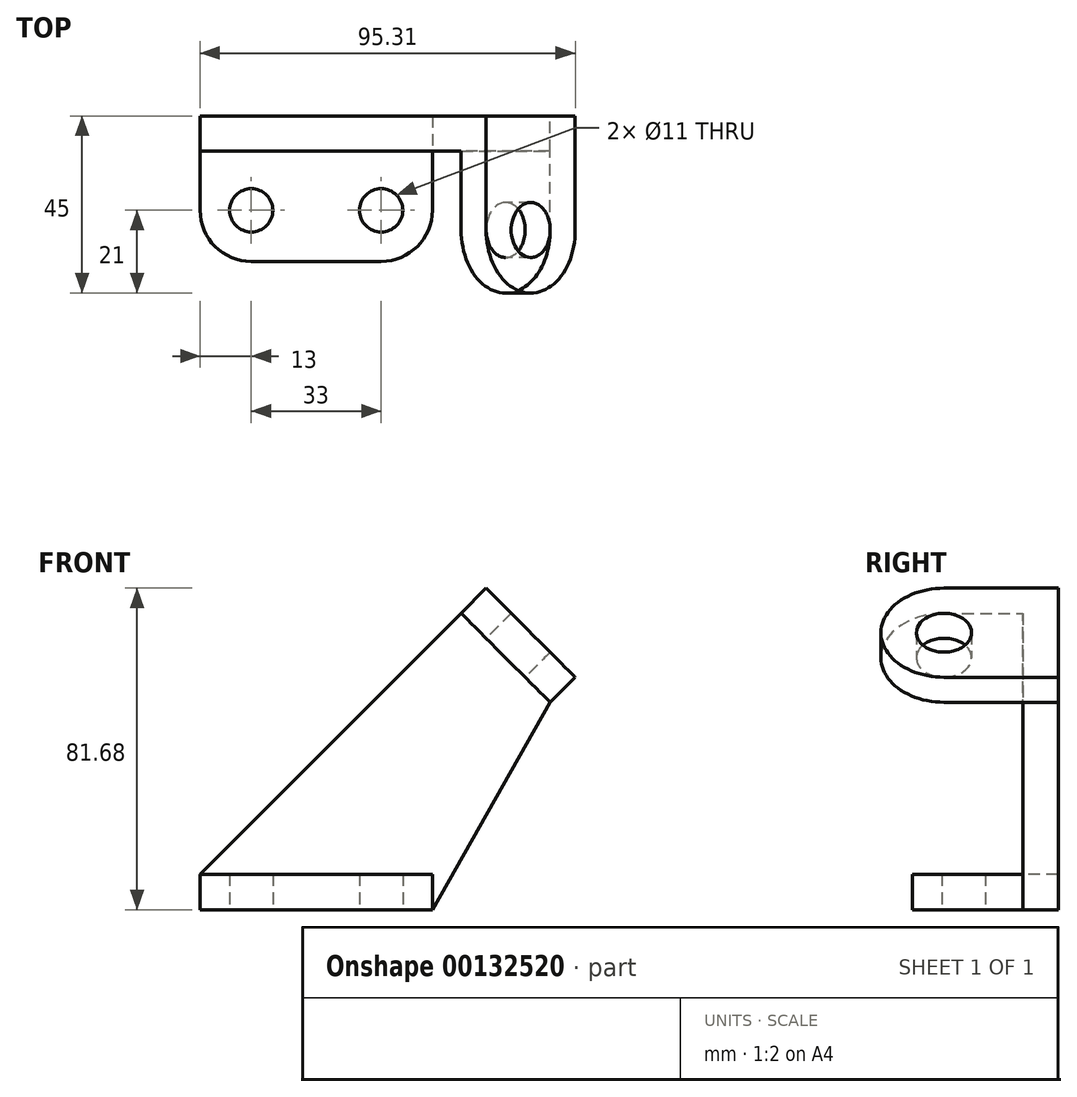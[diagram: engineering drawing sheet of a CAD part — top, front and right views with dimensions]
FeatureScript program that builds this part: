
annotation { "Feature Type Name" : "Feature", "Feature Type Description" : "" }
export const myFeature = defineFeature(function(context is Context, id is Id, definition is map)
    precondition{}
    {
        {
            var Q0;
            Q0=qCreatedBy(makeId("Top.planeOp"),FACE);
            var sketch = newSketch(context, id + "F0", { "sketchPlane" : qUnion([Q0])});
            skCircle(sketch, "E0", {"center": v(0, 0) * mm, "radius": 5.5 * mm});
            skCircle(sketch, "E1", {"center": v(33, 0) * mm, "radius": 5.5 * mm});
            skLineSegment(sketch, "E2", {"start": v(-13, 24) * mm, "end": v(-13, 0) * mm});
            skLineSegment(sketch, "E3", {"start": v(46, 24) * mm, "end": v(46, 0) * mm});
            skArc(sketch, "E4", {"start": v(-13, 0) * mm, "mid": v(-9.2, -9.2) * mm, "end": v(0, -13) * mm});
            skArc(sketch, "E5", {"start": v(33, -13) * mm, "mid": v(42.2, -9.2) * mm, "end": v(46, 0) * mm});
            skLineSegment(sketch, "E6", {"start": v(-13, 24) * mm, "end": v(46, 24) * mm});
            skLineSegment(sketch, "E7", {"start": v(0, -13) * mm, "end": v(33, -13) * mm});
            skSolve(sketch);
        }
        {
            var Q0;
            Q0 = qSketchRegion(id + "F0", true);
            extrude(context, id + "F1", {"entities" : qUnion([Q0]), "depth" : 9 * mm});
        }
        {
            var Q0;
            Q0=makeQuery(id+"F1.opExtrude","SWEPT_FACE",FACE,{"disambiguationData":[OSD([sQuery(id+"F0.wireOp",EDGE,"E6")])]});
            var sketch = newSketch(context, id + "F2", { "sketchPlane" : qUnion([Q0])});
            skPoint(sketch, "E8.0", {"position": v(13, 9) * mm});
            skLineSegment(sketch, "E9", {"start": v(13, 9) * mm, "end": v(-53.31, 75.31) * mm});
            skLineSegment(sketch, "E10", {"start": v(-53.31, 75.31) * mm, "end": v(-75.94, 52.69) * mm});
            skLineSegment(sketch, "E11", {"start": v(-46, 9) * mm, "end": v(13, 9) * mm});
            skLineSegment(sketch, "E12", {"start": v(-75.94, 52.69) * mm, "end": v(-46, 0) * mm});
            skLineSegment(sketch, "E13", {"start": v(-64.63, 64) * mm, "end": v(0, 64) * mm, "construction": true});
            skSolve(sketch);
        }
        {
            var Q0;
            Q0=makeQuery(id+"F2.imprint","IMPRINT",FACE,{"disambiguationData":[TD([[makeQuery(id+"F2.imprint","IMPRINT",EDGE,{"derivedFrom":sQuery(id+"F2.wireOp",EDGE,"E9")}),1.0]])]});
            extrude(context, id + "F3", {"entities" : qUnion([Q0]), "operationType" : NewBodyOperationType.ADD, "oppositeDirection" : true, "depth" : 9 * mm});
        }
        {
            var Q0;
            Q0=makeQuery(id+"F3.opExtrude","SWEPT_FACE",FACE,{"disambiguationData":[OSD([sQuery(id+"F2.wireOp",EDGE,"E10")])]});
            var sketch = newSketch(context, id + "F4", { "sketchPlane" : qUnion([Q0])});
            skLineSegment(sketch, "E14", {"start": v(24, 15.56) * mm, "end": v(-5, 15.56) * mm});
            skArc(sketch, "E15", {"start": v(-5, 15.56) * mm, "mid": v(-21, -0.44) * mm, "end": v(-5, -16.44) * mm});
            skLineSegment(sketch, "E16", {"start": v(24, -16.44) * mm, "end": v(-5, -16.44) * mm});
            skLineSegment(sketch, "E17", {"start": v(24, 15.56) * mm, "end": v(24, -16.44) * mm});
            skCircle(sketch, "E18", {"center": v(-5, -0.44) * mm, "radius": 7 * mm});
            skSolve(sketch);
        }
        {
            var Q0;
            Q0 = qSketchRegion(id + "F4", true);
            extrude(context, id + "F5", {"entities" : qUnion([Q0]), "operationType" : NewBodyOperationType.ADD, "depth" : 9 * mm});
        }
    });
